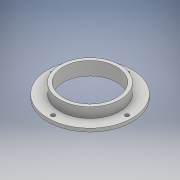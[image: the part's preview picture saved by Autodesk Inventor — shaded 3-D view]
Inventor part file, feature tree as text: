
AUTODESK INVENTOR PART (.ipt)
format: ipt  version: 2018 (Build 220112000, 112)  size: 126,464 bytes
history: native  units: mm
features: extrude x3, sketch x3, other x1, pattern_circular x1
ambient origin geometry x8: Origin, YZ Plane, XZ Plane, XY Plane, X Axis, Y Axis, Z Axis, Center Point
bodies: Body1 (feature_tree)
feature tree (8):
  other  "Sólido1"
  extrude  "Extrusión1"  Depth=3.0mm
  extrude  "Extrusión2"  Depth=9.0mm
  extrude  "Extrusión5"  Depth=10.0mm
  pattern_circular  "Patrón circular1"  [2 undecoded]
  sketch  "Boceto1"  dims[d0=47.7mm d1=3.0mm]
  sketch  "Boceto2"  dims[d2=9.0mm d3=0.0mm d4=75.0mm]
  sketch  "Boceto6"  dims[d5=3.0mm d6=0.0mm d19=3.6mm d20=33.0mm d21=10.0mm d22=0.0mm d23=40.0mm d24=360.0deg]
note: 2 required parameter values undecoded (feature->parameter linkage not recoverable at this tier; creation-order binding heuristic only, values carry confidence <= 0.55)
